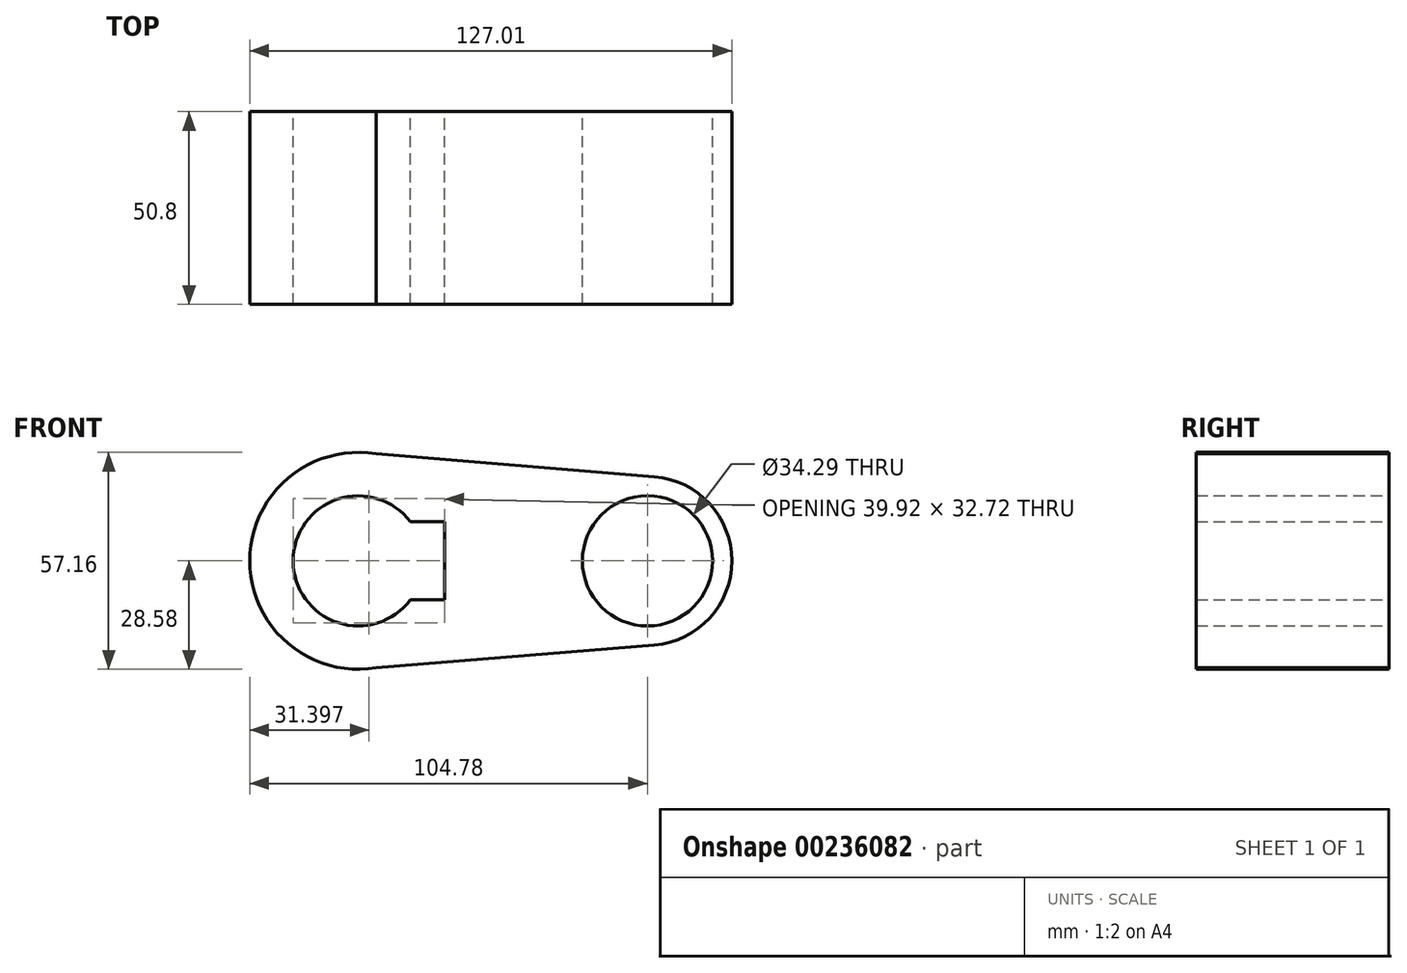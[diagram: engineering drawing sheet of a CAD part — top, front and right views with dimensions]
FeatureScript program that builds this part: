
annotation { "Feature Type Name" : "Feature", "Feature Type Description" : "" }
export const myFeature = defineFeature(function(context is Context, id is Id, definition is map)
    precondition{}
    {
        {
            var Q0;
            Q0=qCreatedBy(makeId("Front.planeOp"),FACE);
            var sketch = newSketch(context, id + "F0", { "sketchPlane" : qUnion([Q0])});
            skCircle(sketch, "E0", {"center": v(0, 0) * mm, "radius": 28.58 * mm});
            skCircle(sketch, "E1", {"center": v(76.2, 0) * mm, "radius": 22.23 * mm});
            skLineSegment(sketch, "E2", {"start": v(0, 28.57) * mm, "end": v(78.02, 22.15) * mm});
            skLineSegment(sketch, "E3", {"start": v(0, -28.57) * mm, "end": v(78.02, -22.15) * mm});
            skCircle(sketch, "E4", {"center": v(0, 0) * mm, "radius": 17.15 * mm});
            skCircle(sketch, "E5", {"center": v(76.2, 0) * mm, "radius": 17.15 * mm});
            skLineSegment(sketch, "E6.left", {"start": v(22.78, 10.27) * mm, "end": v(22.78, -10.27) * mm});
            skLineSegment(sketch, "E7", {"start": v(-13.73, 10.27) * mm, "end": v(-13.73, -10.27) * mm});
            skLineSegment(sketch, "E8", {"start": v(-13.73, 10.27) * mm, "end": v(22.78, 10.27) * mm});
            skLineSegment(sketch, "E9", {"start": v(22.78, -10.27) * mm, "end": v(-13.73, -10.27) * mm});
            skSolve(sketch);
        }
        {
            var Q0;
            Q0 = qSketchRegion(id + "F0", true);
            var Q1;
            {var subQ0=sQuery(id+"F0.wireOp",EDGE,"Ie3rUL3V-FYNA-EtF9-EvLe-xAMHr1mfXxZn.right");Q1=makeQuery(id+"F0.imprint","IMPRINT",FACE,{"disambiguationData":[TD([[makeQuery(id+"F0.imprint","IMPRINT",EDGE,{"derivedFrom":subQ0}),1.0]])]});}
            extrude(context, id + "F1", {"entities" : qUnion([Q0, Q1]), "depth" : 50.8 * mm});
        }
    });
